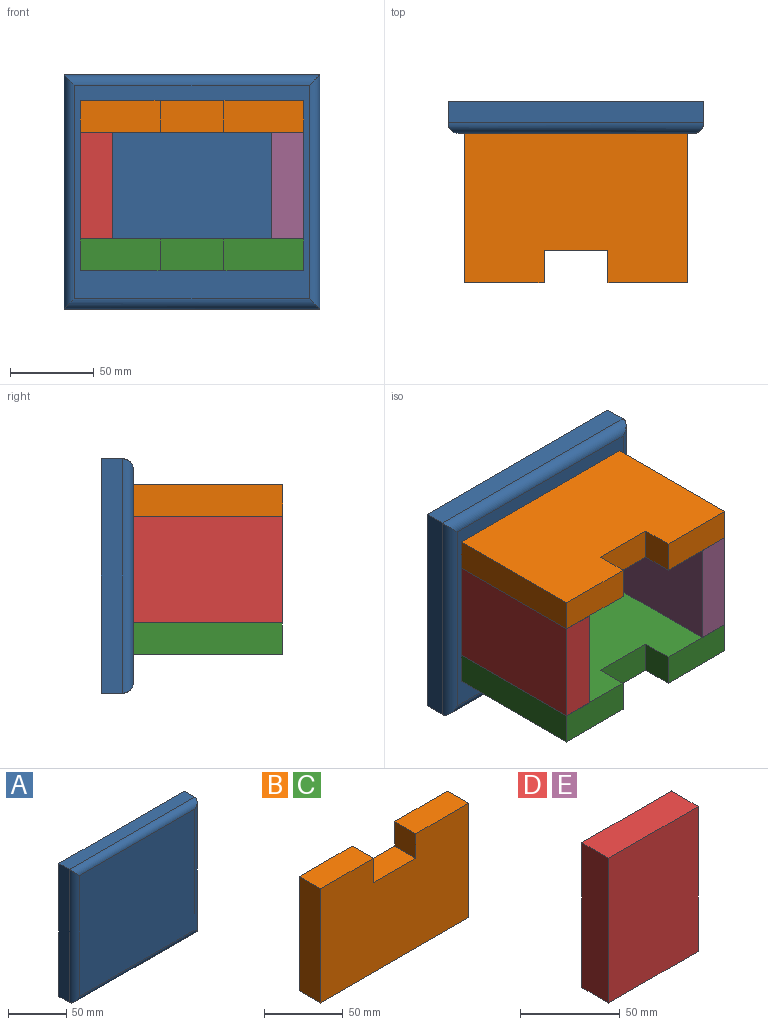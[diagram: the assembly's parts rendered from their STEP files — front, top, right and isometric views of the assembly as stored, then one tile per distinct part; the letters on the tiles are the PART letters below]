
ASSEMBLY  parts=5 mates=6
PART A: 10 faces, bbox 152.4x19.1x139.7 mm
  f0: plane 152.4x12.7mm, normal (0,0,1), area 1935.5mm2, adj f1,f3,f5,f6
  f1: plane 139.7x12.7mm, normal (-1,0,0), area 1774.2mm2, adj f0,f2,f5,f7
  f2: plane 152.4x12.7mm, normal (0,0,-1), area 1935.5mm2, adj f1,f3,f5,f9
  f3: plane 139.7x12.7mm, normal (1,0,0), area 1774.2mm2, adj f0,f2,f5,f8
  f4: plane 139.7x127mm, normal (0,-1,0), area 17741.9mm2, adj f6,f7,f8,f9
  f5: plane 152.4x139.7mm, normal (0,1,0), area 21290.3mm2, adj f0,f1,f2,f3
  f6: cylinder r=6.35mm len=152.4mm, axis (1,0,0), area 1474.1mm2, adj f0,f4,f7,f8
  f7: cylinder r=6.35mm len=139.7mm, axis (0,0,1), area 1347.4mm2, adj f1,f4,f6,f9
  f8: cylinder r=6.35mm len=139.7mm, axis (0,0,-1), area 1347.4mm2, adj f3,f4,f6,f9
  f9: cylinder r=6.35mm len=152.4mm, axis (-1,0,0), area 1474.1mm2, adj f2,f4,f7,f8
PART B: 10 faces, bbox 133.4x19.1x88.9 mm
  f0: plane 47.63x19.05mm, normal (0,0,1), area 907.3mm2, adj f1,f7,f8,f9
  f1: plane 19.05x19.05mm, normal (-1,0,0), area 362.9mm2, adj f0,f2,f8,f9
  f2: plane 38.1x19.05mm, normal (0,0,1), area 725.8mm2, adj f1,f3,f8,f9
  f3: plane 19.05x19.05mm, normal (1,0,0), area 362.9mm2, adj f2,f4,f8,f9
  f4: plane 47.63x19.05mm, normal (0,0,1), area 907.3mm2, adj f3,f5,f8,f9
  f5: plane 88.9x19.05mm, normal (-1,0,0), area 1693.5mm2, adj f4,f6,f8,f9
  f6: plane 133.35x19.05mm, normal (0,0,-1), area 2540.3mm2, adj f5,f7,f8,f9
  f7: plane 88.9x19.05mm, normal (1,0,0), area 1693.5mm2, adj f0,f6,f8,f9
  f8: plane 133.35x88.9mm, normal (0,-1,0), area 11129mm2, adj f0,f1,f2,f3,f4,f5,f6,f7
  f9: plane 133.35x88.9mm, normal (0,1,0), area 11129mm2, adj f0,f1,f2,f3,f4,f5,f6,f7
PART C: same geometry as B
PART D: 6 faces, bbox 63.5x19.1x88.9 mm
  f0: plane 63.5x19.05mm, normal (0,0,1), area 1209.7mm2, adj f1,f3,f4,f5
  f1: plane 88.9x19.05mm, normal (-1,0,0), area 1693.5mm2, adj f0,f2,f4,f5
  f2: plane 63.5x19.05mm, normal (0,0,-1), area 1209.7mm2, adj f1,f3,f4,f5
  f3: plane 88.9x19.05mm, normal (1,0,0), area 1693.5mm2, adj f0,f2,f4,f5
  f4: plane 88.9x63.5mm, normal (0,-1,0), area 5645.2mm2, adj f0,f1,f2,f3
  f5: plane 88.9x63.5mm, normal (0,1,0), area 5645.2mm2, adj f0,f1,f2,f3
PART E: same geometry as D
PLACE A t=(82.23,202.11,-9.94)mm
PLACE B rot(axis=(0,-0.71,0.71),180deg) t=(96.14,145.63,25.78)mm
PLACE C rot(axis=(1,0,0),90deg) t=(68.92,145.76,-37.72)mm
PLACE D rot(axis=(-0.58,-0.58,-0.58),120deg) t=(34.91,112.61,52.89)mm
PLACE E rot(axis=(-0.58,-0.58,-0.58),120deg) t=(149.21,112.61,52.89)mm
MATE planar D.f2 <-> B.f0  axis (0,-1,0) through (25.39,94.04,-5.97)mm
MATE planar B.f9 <-> E.f3  axis (0,0,-1) through (82.54,140.77,25.78)mm
MATE planar B.f9 <-> D.f3  axis (0,0,-1) through (82.54,140.77,25.78)mm
MATE planar A.f4 <-> C.f6  axis (0,-1,0) through (82.52,183.06,-9.74)mm
MATE planar B.f7 <-> D.f4  axis (-1,0,0) through (15.86,138.49,35.31)mm
MATE planar E.f5 <-> B.f5  axis (1,0,0) through (149.21,138.49,-5.97)mm
